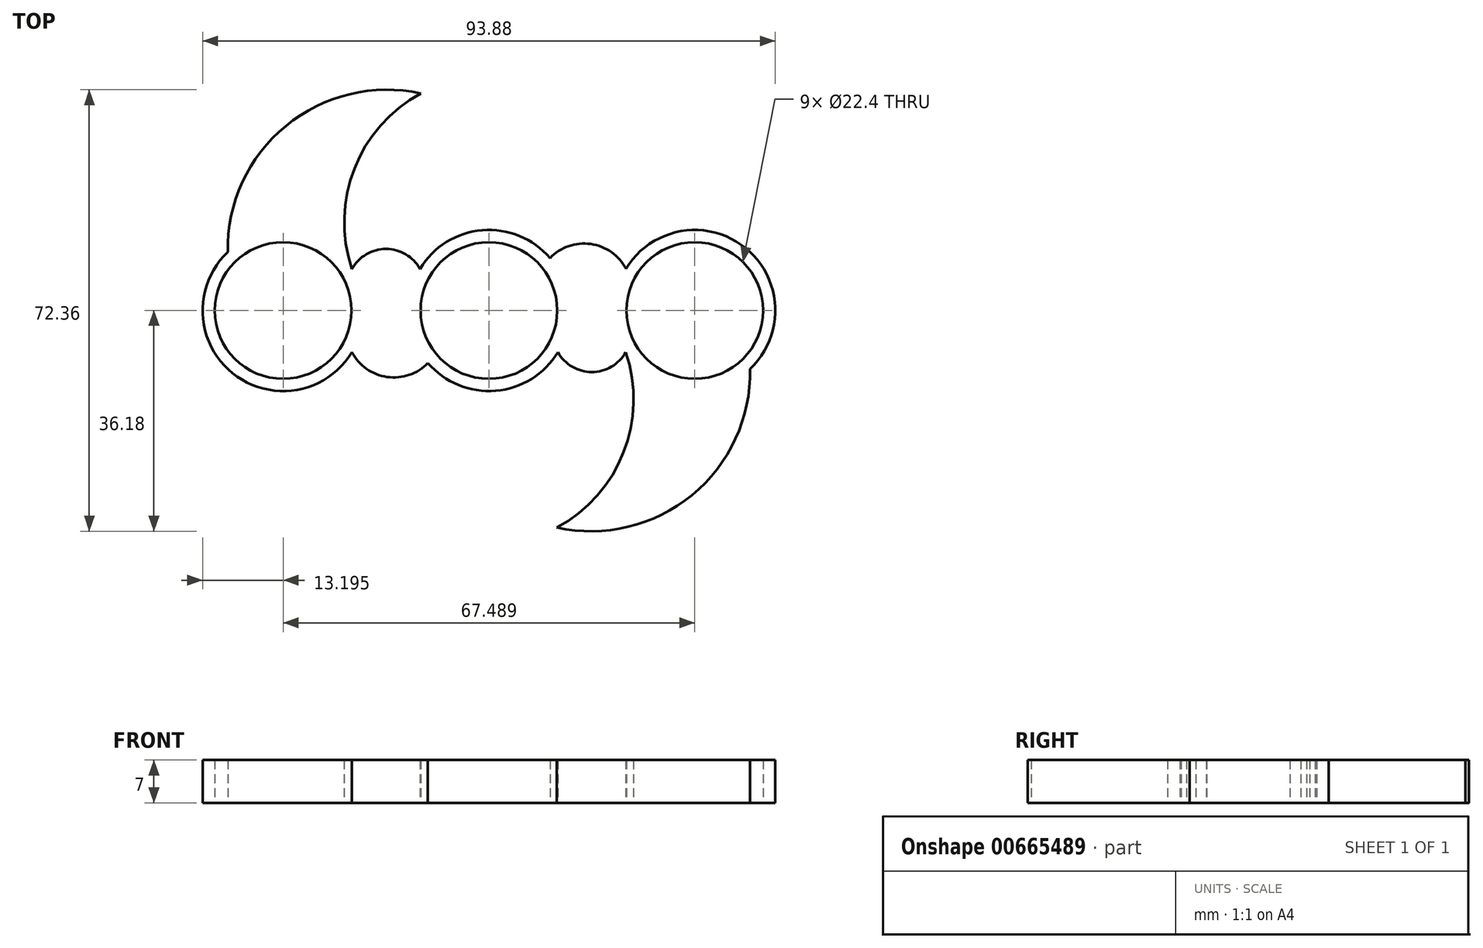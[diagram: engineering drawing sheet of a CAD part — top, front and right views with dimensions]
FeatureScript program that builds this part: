
annotation { "Feature Type Name" : "Feature", "Feature Type Description" : "" }
export const myFeature = defineFeature(function(context is Context, id is Id, definition is map)
    precondition{}
    {
        {
            var Q0;
            Q0=qCreatedBy(makeId("Top.planeOp"),FACE);
            var sketch = newSketch(context, id + "F0", { "sketchPlane" : qUnion([Q0])});
            skCircle(sketch, "E0", {"center": v(0, 0) * mm, "radius": 11.2 * mm});
            skArc(sketch, "E1", {"start": v(-10, -8.6) * mm, "mid": v(1.1, -13.15) * mm, "end": v(11.3, -6.83) * mm});
            skCircle(sketch, "E2", {"center": v(-33.74, 0) * mm, "radius": 11.2 * mm});
            skArc(sketch, "E3", {"start": v(-42.82, 9.59) * mm, "mid": v(-42.04, -10.27) * mm, "end": v(-22.46, -6.85) * mm});
            skCircle(sketch, "E4", {"center": v(33.74, 0) * mm, "radius": 11.2 * mm});
            skArc(sketch, "E5", {"start": v(42.82, -9.59) * mm, "mid": v(42.04, 10.27) * mm, "end": v(22.46, 6.85) * mm});
            skArc(sketch, "E6", {"start": v(-11.15, 35.58) * mm, "mid": v(-33.28, 30.26) * mm, "end": v(-42.82, 9.59) * mm});
            skArc(sketch, "E7", {"start": v(-11.15, 35.58) * mm, "mid": v(-22.06, 23.27) * mm, "end": v(-22.45, 6.83) * mm});
            skArc(sketch, "E8.1.0", {"start": v(11.15, -35.58) * mm, "mid": v(33.28, -30.26) * mm, "end": v(42.82, -9.59) * mm});
            skArc(sketch, "E8.1.1", {"start": v(11.15, -35.58) * mm, "mid": v(22.06, -23.27) * mm, "end": v(22.45, -6.83) * mm});
            skArc(sketch, "E9", {"start": v(-11.3, 6.83) * mm, "mid": v(-16.87, 10.08) * mm, "end": v(-22.45, 6.83) * mm});
            skArc(sketch, "E10.1.0", {"start": v(11.3, -6.83) * mm, "mid": v(16.87, -10.08) * mm, "end": v(22.45, -6.83) * mm});
            skArc(sketch, "E11", {"start": v(-22.46, -6.85) * mm, "mid": v(-16.68, -10.9) * mm, "end": v(-10, -8.6) * mm});
            skArc(sketch, "E12.1.0", {"start": v(22.46, 6.85) * mm, "mid": v(16.68, 10.9) * mm, "end": v(10, 8.6) * mm});
            skArc(sketch, "E13.trimOffspring", {"start": v(10, 8.6) * mm, "mid": v(-1.1, 13.15) * mm, "end": v(-11.3, 6.83) * mm});
            skSolve(sketch);
        }
        {
            var Q0;
            Q0=makeQuery(id+"F0.imprint","IMPRINT",FACE,{"disambiguationData":[TD([[makeQuery(id+"F0.imprint","IMPRINT",EDGE,{"derivedFrom":sQuery(id+"F0.wireOp",EDGE,"E0")}),-1.0]])]});
            extrude(context, id + "F1", {"entities" : qUnion([Q0]), "depth" : 7 * mm, "offsetDistance" : 25 * mm});
        }
    });
